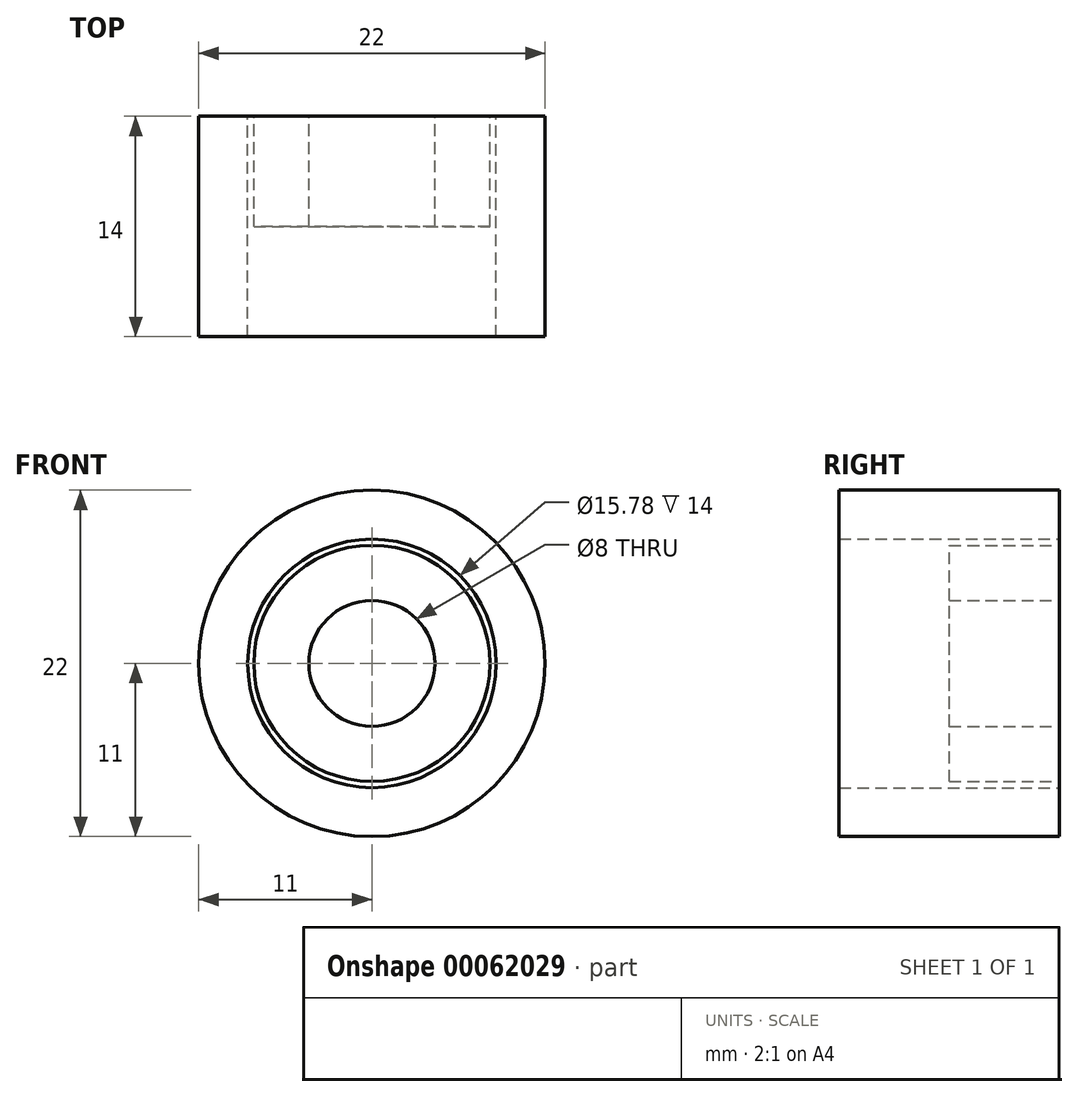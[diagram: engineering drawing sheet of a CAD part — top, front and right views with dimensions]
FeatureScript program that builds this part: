
annotation { "Feature Type Name" : "Feature", "Feature Type Description" : "" }
export const myFeature = defineFeature(function(context is Context, id is Id, definition is map)
    precondition{}
    {
        {
            var Q0;
            Q0=qCreatedBy(makeId("Front.planeOp"),FACE);
            var sketch = newSketch(context, id + "F0", { "sketchPlane" : qUnion([Q0])});
            skCircle(sketch, "E0", {"center": v(0, 0) * mm, "radius": 11 * mm});
            skCircle(sketch, "E1", {"center": v(0, 0) * mm, "radius": 4 * mm});
            skCircle(sketch, "E2", {"center": v(0, 0) * mm, "radius": 7.5 * mm});
            skSolve(sketch);
        }
        {
            var Q0;
            Q0=makeQuery(id+"F0.imprint","IMPRINT",FACE,{"disambiguationData":[TD([[makeQuery(id+"F0.imprint","IMPRINT",EDGE,{"derivedFrom":sQuery(id+"F0.wireOp",EDGE,"E1")}),-1.0]])]});
            extrude(context, id + "F1", {"entities" : qUnion([Q0]), "depth" : 7 * mm});
        }
        {
            var Q0;
            Q0=qCreatedBy(makeId("Front.planeOp"),FACE);
            var sketch = newSketch(context, id + "F2", { "sketchPlane" : qUnion([Q0])});
            skCircle(sketch, "E3", {"center": v(0, 0) * mm, "radius": 11 * mm});
            skCircle(sketch, "E4", {"center": v(0, 0) * mm, "radius": 7.9 * mm});
            skSolve(sketch);
        }
        {
            var Q0;
            Q0=makeQuery(id+"F2.imprint","IMPRINT",FACE,{"disambiguationData":[TD([[makeQuery(id+"F2.imprint","IMPRINT",EDGE,{"derivedFrom":sQuery(id+"F2.wireOp",EDGE,"E3")}),1.0]])]});
            extrude(context, id + "F3", {"entities" : qUnion([Q0]), "operationType" : NewBodyOperationType.ADD, "depth" : 7 * mm});
        }
        {
            var Q0;
            Q0 = qSketchRegion(id + "F2", true);
            var Q1;
            Q1=makeQuery(id+"F3.opExtrude","CAP_FACE",FACE,{"disambiguationData":[OSD([sQuery(id+"F2.wireOp",EDGE,"E3"),sQuery(id+"F2.wireOp",EDGE,"E4")])],"isStart":false});
            extrude(context, id + "F4", {"entities" : qUnion([Q0, Q1]), "operationType" : NewBodyOperationType.ADD, "depth" : 7 * mm});
        }
    });
